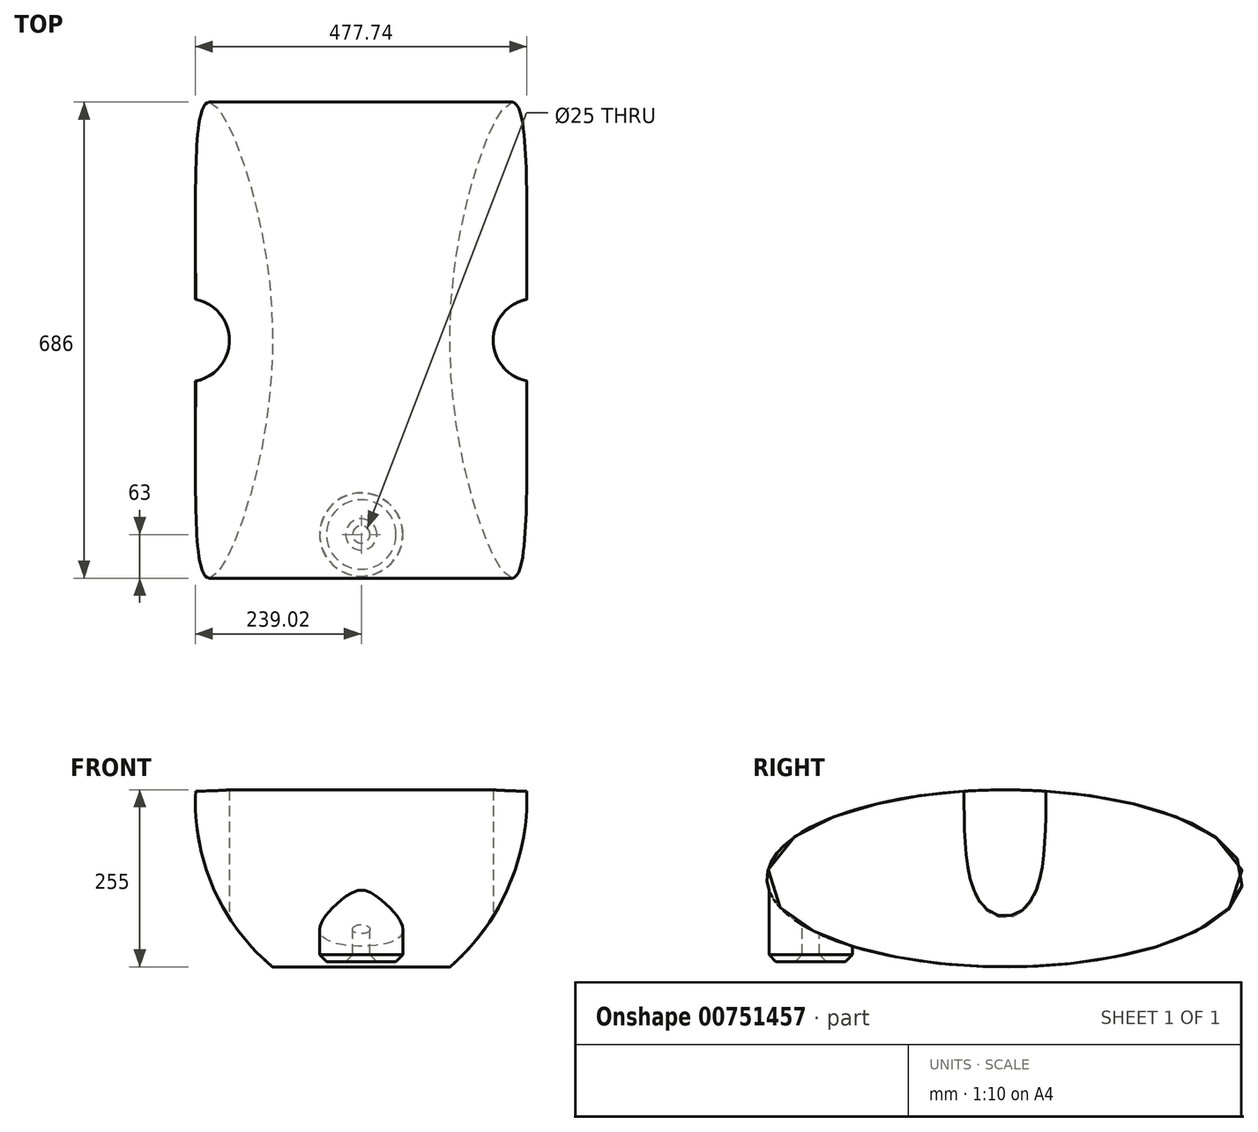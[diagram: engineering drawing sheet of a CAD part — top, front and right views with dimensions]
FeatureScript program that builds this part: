
annotation { "Feature Type Name" : "Feature", "Feature Type Description" : "" }
export const myFeature = defineFeature(function(context is Context, id is Id, definition is map)
    precondition{}
    {
        {
            var Q0;
            Q0=qCreatedBy(makeId("Front.planeOp"),FACE);
            var sketch = newSketch(context, id + "F0", { "sketchPlane" : qUnion([Q0])});
            skLineSegment(sketch, "E0.bottom", {"start": v(127.8, -127.5) * mm, "end": v(-127.8, -127.5) * mm});
            skLineSegment(sketch, "E0.top", {"start": v(238.5, 127.5) * mm, "end": v(-238.5, 127.5) * mm});
            skPoint(sketch, "E0.middle", {"position": v(0, 0) * mm});
            skLineSegment(sketch, "E1", {"start": v(0, 127.5) * mm, "end": v(0, -127.5) * mm, "construction": true});
            skPoint(sketch, "E2.orphan", {"position": v(-238.5, -127.5) * mm});
            skPoint(sketch, "E3.orphan", {"position": v(238.5, -127.5) * mm});
            skArc(sketch, "E4", {"start": v(-238.5, 127.5) * mm, "mid": v(-213.5, -13.18) * mm, "end": v(-127.8, -127.5) * mm});
            skArc(sketch, "E5", {"start": v(127.8, -127.5) * mm, "mid": v(212.13, -12.58) * mm, "end": v(238.5, 127.5) * mm});
            skSolve(sketch);
        }
        {
            var Q0;
            Q0=makeQuery(id+"F0.imprint","IMPRINT",FACE,{"disambiguationData":[TD([[makeQuery(id+"F0.imprint","IMPRINT",EDGE,{"derivedFrom":sQuery(id+"F0.wireOp",EDGE,"E0.bottom")}),-1.0]])]});
            extrude(context, id + "F1", {"entities" : qUnion([Q0]), "endBound" : BoundingType.SYMMETRIC, "depth" : 686 * mm, "offsetDistance" : 25 * mm});
        }
        {
            var Q0;
            Q0=qCreatedBy(makeId("Right.planeOp"),FACE);
            var sketch = newSketch(context, id + "F2", { "sketchPlane" : qUnion([Q0])});
            skEllipse(sketch, "E6", {"center": v(0, 0) * mm, "majorRadius": 343 * mm, "minorRadius": 127.5 * mm, "majorAxis": v(1, 0)});
            skSolve(sketch);
        }
        {
            var Q0;
            Q0 = qSketchRegion(id + "F2", true);
            var Q1;
            Q1=makeQuery(id+"F1.opExtrude","SWEPT_FACE",FACE,{"disambiguationData":[OSD([sQuery(id+"F0.wireOp",EDGE,"80370af4-3491-47ec-9c7e-19e747b012f40.MirrorCS")])]});
            extrude(context, id + "F3", {"entities" : qUnion([Q0]), "operationType" : NewBodyOperationType.INTERSECT, "endBound" : BoundingType.THROUGH_ALL, "depth" : 65 * mm, "offsetDistance" : 25 * mm, "hasSecondDirection" : true, "secondDirectionBound" : SecondDirectionBoundingType.THROUGH_ALL, "secondDirectionOppositeDirection" : true, "secondDirectionDepth" : 25 * mm, "secondDirectionBoundEntityFace" : qUnion([Q1])});
        }
        {
            var Q0;
            Q0=qCreatedBy(makeId("Right.planeOp"),FACE);
            var sketch = newSketch(context, id + "F4", { "sketchPlane" : qUnion([Q0])});
            skCircle(sketch, "E7", {"center": v(0, 0) * mm, "radius": 500 * mm});
            skSolve(sketch);
        }
        {
            var Q0;
            Q0=makeQuery(id+"F1.opExtrude","SWEPT_BODY",BODY,{"disambiguationData":[OSD([sQuery(id+"F0.wireOp",EDGE,"E0.bottom"),sQuery(id+"F0.wireOp",EDGE,"E0.top"),sQuery(id+"F0.wireOp",EDGE,"6bdbb09c-85a1-4aaf-a778-ba107cdfbe8e"),sQuery(id+"F0.wireOp",EDGE,"80370af4-3491-47ec-9c7e-19e747b012f40.MirrorCS")])]});
            var Q1;
            Q1=makeQuery(id+"F0.imprint","IMPRINT",FACE,{"disambiguationData":[TD([[makeQuery(id+"F0.imprint","IMPRINT",EDGE,{"derivedFrom":sQuery(id+"F0.wireOp",EDGE,"E0.bottom")}),-1.0]])]});
            mirror(context, id + "F5", {"operationType" : NewBodyOperationType.ADD, "entities" : qUnion([Q0]), "mirrorPlane" : qUnion([Q1])});
        }
        {
            var Q0;
            Q0=qCreatedBy(makeId("Top.planeOp"),FACE);
            var sketch = newSketch(context, id + "F6", { "sketchPlane" : qUnion([Q0])});
            skCircle(sketch, "E8", {"center": v(0, -280) * mm, "radius": 60 * mm});
            skCircle(sketch, "E9", {"center": v(0, -280) * mm, "radius": 12.5 * mm});
            skSolve(sketch);
        }
        {
            var Q0;
            Q0 = qSketchRegion(id + "F6", true);
            var Q1;
            Q1=makeQuery(id+"F3.boolean.opBoolean","COPY",FACE,{"derivedFrom":makeQuery(id+"F3.boolean.toolComplement.opBoolean","COPY",FACE,{"derivedFrom":makeQuery(id+"F3.opExtrude","SWEPT_FACE",FACE,{"disambiguationData":[OSD([sQuery(id+"F2.wireOp",EDGE,"E6")])]})})});
            extrude(context, id + "F7", {"entities" : qUnion([Q0]), "operationType" : NewBodyOperationType.ADD, "oppositeDirection" : true, "depth" : 120 * mm, "endBoundEntityFace" : qUnion([Q1]), "hasOffset" : true, "offsetDistance" : 50 * mm});
        }
        {
            var Q0;
            Q0=qCreatedBy(makeId("Top.planeOp"),FACE);
            var sketch = newSketch(context, id + "F8", { "sketchPlane" : qUnion([Q0])});
            skCircle(sketch, "E10", {"center": v(-250, 0) * mm, "radius": 60 * mm});
            skLineSegment(sketch, "E11", {"start": v(0, -257.36) * mm, "end": v(0, 174.35) * mm, "construction": true});
            skCircle(sketch, "E12.MirrorC", {"center": v(250, 0) * mm, "radius": 60 * mm});
            skSolve(sketch);
        }
        {
            var Q0;
            Q0 = qSketchRegion(id + "F8", true);
            var Q1;
            Q1=makeQuery(id+"F1.opExtrude","SWEPT_BODY",BODY,{"disambiguationData":[OSD([sQuery(id+"F0.wireOp",EDGE,"E0.bottom"),sQuery(id+"F0.wireOp",EDGE,"E0.top"),sQuery(id+"F0.wireOp",EDGE,"6bdbb09c-85a1-4aaf-a778-ba107cdfbe8e"),sQuery(id+"F0.wireOp",EDGE,"80370af4-3491-47ec-9c7e-19e747b012f40.MirrorCS")])]});
            extrude(context, id + "F9", {"entities" : qUnion([Q0]), "operationType" : NewBodyOperationType.REMOVE, "endBound" : BoundingType.THROUGH_ALL, "depth" : 25 * mm, "endBoundEntityBody" : qUnion([Q1]), "offsetDistance" : 25 * mm, "hasSecondDirection" : true, "secondDirectionBound" : SecondDirectionBoundingType.THROUGH_ALL, "secondDirectionOppositeDirection" : true, "secondDirectionDepth" : 25 * mm});
        }
        {
            var Q0;
            Q0=makeQuery(id+"F7.opExtrude","CAP_FACE",FACE,{"disambiguationData":[OSD([sQuery(id+"F6.wireOp",EDGE,"E8"),sQuery(id+"F6.wireOp",EDGE,"E9")])],"isStart":false});
            chamfer(context, id + "F10", {"entities" : qUnion([Q0]), "width" : 10 * mm, "tangentPropagation" : true});
        }
    });
